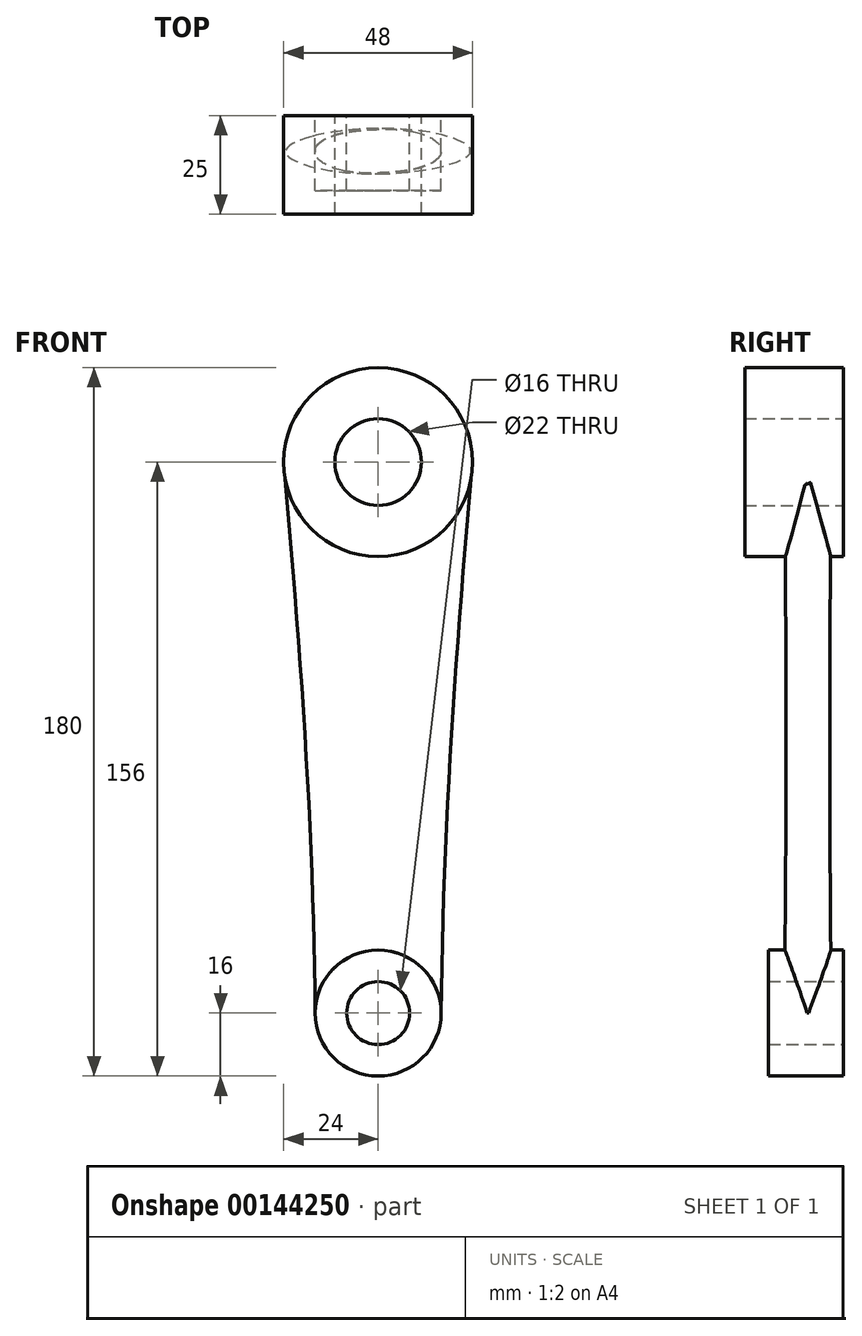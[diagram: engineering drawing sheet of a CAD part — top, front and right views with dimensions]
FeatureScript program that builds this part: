
annotation { "Feature Type Name" : "Feature", "Feature Type Description" : "" }
export const myFeature = defineFeature(function(context is Context, id is Id, definition is map)
    precondition{}
    {
        {
            var Q0;
            Q0=qCreatedBy(makeId("Front.planeOp"),FACE);
            var sketch = newSketch(context, id + "F0", { "sketchPlane" : qUnion([Q0])});
            skCircle(sketch, "E0", {"center": v(0, 0) * mm, "radius": 8 * mm});
            skCircle(sketch, "E1", {"center": v(0, 140) * mm, "radius": 11 * mm});
            skLineSegment(sketch, "E2", {"start": v(0, 140) * mm, "end": v(0, 0) * mm, "construction": true});
            skCircle(sketch, "E3", {"center": v(0, 140) * mm, "radius": 24 * mm});
            skCircle(sketch, "E4", {"center": v(0, 0) * mm, "radius": 16 * mm});
            skLineSegment(sketch, "E5", {"start": v(-23.96, 138.63) * mm, "end": v(-16.03, 0) * mm});
            skLineSegment(sketch, "E6", {"start": v(23.96, 138.63) * mm, "end": v(16.03, 0) * mm});
            skSolve(sketch);
        }
        {
            var Q0;
            Q0=makeQuery(id+"F0.imprint","IMPRINT",FACE,{"disambiguationData":[TD([[makeQuery(id+"F0.imprint","IMPRINT",EDGE,{"derivedFrom":sQuery(id+"F0.wireOp",EDGE,"E0")}),-1.0]])]});
            extrude(context, id + "F1", {"entities" : qUnion([Q0]), "depth" : 19 * mm});
        }
        {
            var Q0;
            Q0=qCreatedBy(makeId("Top.planeOp"),FACE);
            var sketch = newSketch(context, id + "F2", { "sketchPlane" : qUnion([Q0])});
            skLineSegment(sketch, "E7", {"start": v(-16, -19) * mm, "end": v(-16.03, 0) * mm, "construction": true});
            skLineSegment(sketch, "E8", {"start": v(16, 0) * mm, "end": v(16, -19) * mm, "construction": true});
            skLineSegment(sketch, "E9.0", {"start": v(16, 0) * mm, "end": v(-16.03, 0) * mm, "construction": true});
            skLineSegment(sketch, "E10.0", {"start": v(16, -19) * mm, "end": v(-16, -19) * mm, "construction": true});
            skEllipse(sketch, "E11", {"center": v(0, -9) * mm, "majorRadius": 16.01 * mm, "minorRadius": 6 * mm, "majorAxis": v(-1, 0)});
            skPoint(sketch, "E12", {"position": v(0, -3) * mm});
            skSolve(sketch);
        }
        {
            var Q0;
            Q0=makeQuery(id+"F0.imprint","IMPRINT",FACE,{"disambiguationData":[TD([[makeQuery(id+"F0.imprint","IMPRINT",EDGE,{"derivedFrom":sQuery(id+"F0.wireOp",EDGE,"E1")}),-1.0]])]});
            extrude(context, id + "F3", {"entities" : qUnion([Q0]), "depth" : 25 * mm});
        }
        {
            var Q0;
            Q0=sQuery(id+"F0.wireOp",VERTEX,"E3.center");
            var Q1;
            Q1=qCreatedBy(makeId("Top.planeOp"),FACE);
            cPlane(context, id + "F4", {"entities" : qUnion([Q0, Q1]), "cplaneType" : CPlaneType.PLANE_POINT, "offset" : 25 * mm, "width" : 150 * mm, "height" : 150 * mm});
        }
        {
            var Q0;
            Q0=qCreatedBy(id+"F4.planeOp",FACE);
            var sketch = newSketch(context, id + "F5", { "sketchPlane" : qUnion([Q0])});
            skEllipse(sketch, "E13", {"center": v(0, -9) * mm, "majorRadius": 24 * mm, "minorRadius": 6 * mm, "majorAxis": v(-1, 0)});
            skPoint(sketch, "E14", {"position": v(0, -3) * mm});
            skLineSegment(sketch, "E15", {"start": v(24, 0) * mm, "end": v(24, -25) * mm, "construction": true});
            skSolve(sketch);
        }
        {
            var Q0;
            Q0=makeQuery(id+"F2.imprint","IMPRINT",FACE,{"disambiguationData":[TD([[makeQuery(id+"F2.imprint","IMPRINT",EDGE,{"derivedFrom":sQuery(id+"F2.wireOp",EDGE,"E11")}),1.0]])]});
            var Q1;
            Q1=makeQuery(id+"F5.imprint","IMPRINT",FACE,{"disambiguationData":[TD([[makeQuery(id+"F5.imprint","IMPRINT",EDGE,{"derivedFrom":sQuery(id+"F5.wireOp",EDGE,"E13")}),1.0]])]});
            loft(context, id + "F6", {"operationType" : NewBodyOperationType.ADD, "sheetProfilesArray" : [{ "sheetProfileEntities" : qUnion([Q0]) }, { "sheetProfileEntities" : qUnion([Q1]) }]});
        }
        {
            var Q0;
            Q0=qCreatedBy(makeId("Front.planeOp"),FACE);
            var sketch = newSketch(context, id + "F7", { "sketchPlane" : qUnion([Q0])});
            skCircle(sketch, "E16.0", {"center": v(0, 140) * mm, "radius": 11 * mm});
            skCircle(sketch, "E17.0", {"center": v(0, 0) * mm, "radius": 8 * mm});
            skSolve(sketch);
        }
        {
            var Q0;
            Q0 = qSketchRegion(id + "F7", true);
            extrude(context, id + "F8", {"entities" : qUnion([Q0]), "operationType" : NewBodyOperationType.REMOVE, "endBound" : BoundingType.THROUGH_ALL, "depth" : 25 * mm});
        }
    });
